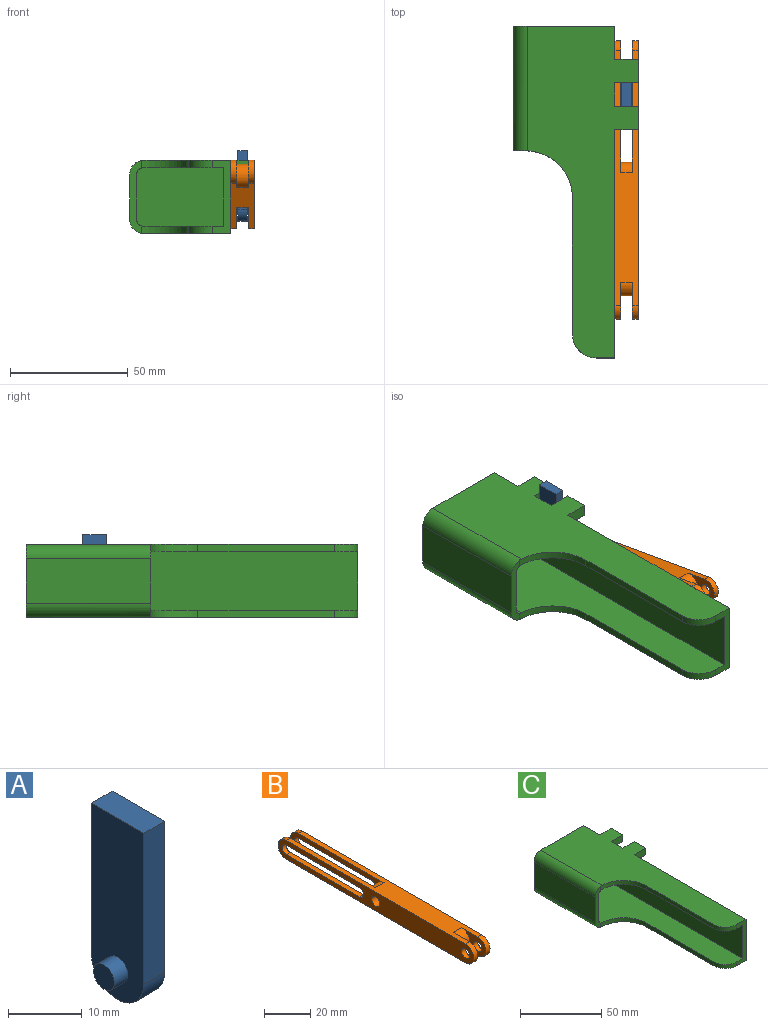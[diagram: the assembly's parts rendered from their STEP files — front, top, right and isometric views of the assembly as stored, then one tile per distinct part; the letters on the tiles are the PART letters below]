
ASSEMBLY  parts=3 mates=3
PART A: 10 faces, bbox 9.2x10x30 mm
  f0: plane 25x4mm, normal (0,1,0), area 100mm2, adj f1,f3,f4,f9
  f1: plane 30x10mm, normal (-1,0,0), area 276.7mm2, adj f0,f2,f4,f7,f9
  f2: plane 25x4mm, normal (0,-1,0), area 100mm2, adj f1,f3,f4,f9
  f3: plane 30x10mm, normal (1,0,0), area 276.7mm2, adj f0,f2,f4,f6,f9
  f4: plane 10x4mm, normal (0,0,1), area 40mm2, adj f0,f1,f2,f3
  f5: plane 4x4mm, normal (1,0,0), area 12.6mm2, adj f6
  f6: cylinder r=2mm len=4mm, axis (-1,0,0), area 32.7mm2, adj f3,f5
  f7: cylinder r=2mm len=4mm, axis (-1,0,0), area 32.7mm2, adj f1,f8
  f8: plane 4x4mm, normal (-1,0,0), area 12.6mm2, adj f7
  f9: cylinder r=5mm len=10mm, axis (-1,0,0), area 62.8mm2, adj f0,f1,f2,f3
PART B: 25 faces, bbox 10x120x10 mm
  f0: plane 110x10mm, normal (0,0,1), area 787.5mm2, adj f1,f2,f9,f15,f16,f17,f18,f19
  f1: cylinder r=5mm len=10mm, axis (-1,0,0), area 39.3mm2, adj f0,f3,f16,f20
  f2: cylinder r=5mm len=10mm, axis (-1,0,0), area 39.3mm2, adj f0,f3,f17,f21
  f3: plane 110x10mm, normal (0,0,-1), area 787.5mm2, adj f1,f2,f9,f15,f16,f17,f18,f19
  f4: cylinder r=2.5mm len=5mm, axis (-1,0,0), area 19.6mm2, adj f5,f7,f16,f18
  f5: plane 45x2.5mm, normal (0,0,-1), area 112.5mm2, adj f4,f6,f16,f18
  f6: cylinder r=2.5mm len=5mm, axis (-1,0,0), area 19.6mm2, adj f5,f7,f16,f18
  f7: plane 45x2.5mm, normal (0,0,1), area 112.5mm2, adj f4,f6,f16,f18
  f8: cylinder r=2.5mm len=5mm, axis (-1,0,0), area 39.3mm2, adj f16,f20
  f9: cylinder r=5mm len=10mm, axis (-1,0,0), area 39.3mm2, adj f0,f3,f16,f18
  f10: cylinder r=2.5mm len=5mm, axis (-1,0,0), area 19.6mm2, adj f11,f13,f17,f19
  f11: plane 45x2.5mm, normal (0,0,-1), area 112.5mm2, adj f10,f12,f17,f19
  f12: cylinder r=2.5mm len=5mm, axis (-1,0,0), area 19.6mm2, adj f11,f13,f17,f19
  f13: plane 45x2.5mm, normal (0,0,1), area 112.5mm2, adj f10,f12,f17,f19
  f14: cylinder r=2.5mm len=5mm, axis (-1,0,0), area 39.3mm2, adj f17,f21
  f15: cylinder r=5mm len=10mm, axis (-1,0,0), area 39.3mm2, adj f0,f3,f17,f19
  f16: plane 120x10mm, normal (1,0,0), area 894.6mm2, adj f0,f1,f3,f4,f5,f6,f7,f8
  f17: plane 120x10mm, normal (-1,0,0), area 894.6mm2, adj f0,f2,f3,f10,f11,f12,f13,f14
  f18: plane 57.5x10mm, normal (-1,0,0), area 280.4mm2, adj f0,f3,f4,f5,f6,f7,f9,f24
  f19: plane 57.5x10mm, normal (1,0,0), area 280.4mm2, adj f0,f3,f10,f11,f12,f13,f15,f24
  f20: plane 15x10mm, normal (-1,0,0), area 80.4mm2, adj f0,f1,f3,f8,f23
  f21: plane 15x10mm, normal (1,0,0), area 80.4mm2, adj f0,f2,f3,f14,f23
  f22: cylinder r=2.5mm len=10mm, axis (1,0,0), area 157.1mm2, adj f16,f17
  f23: cylinder r=5mm len=10mm, axis (-1,0,0), area 78.5mm2, adj f0,f3,f20,f21
  f24: cylinder r=5mm len=10mm, axis (1,0,0), area 78.5mm2, adj f0,f3,f18,f19
PART C: 32 faces, bbox 53x141x31 mm
  f0: plane 141x31mm, normal (1,0,0), area 4258.4mm2, adj f1,f2,f4,f5,f22,f24,f25,f26
  f1: plane 31x8mm, normal (0,-1,0), area 123mm2, adj f0,f4,f5,f10,f11,f12,f20,f21
  f2: plane 43x31mm, normal (0,1,0), area 1317.5mm2, adj f0,f3,f4,f5,f6,f7
  f3: plane 53x19mm, normal (-1,0,0), area 1007mm2, adj f2,f6,f7,f19
  f4: plane 141x47mm, normal (0,0,1), area 3809.4mm2, adj f0,f1,f2,f7,f16,f18,f20,f24
  f5: plane 141x37mm, normal (0,0,-1), area 3609.4mm2, adj f0,f1,f2,f6,f15,f17,f21
  f6: cylinder r=6mm len=53.03mm, axis (0,-1,0), area 499.5mm2, adj f2,f3,f5,f17,f19
  f7: cylinder r=6mm len=53.03mm, axis (0,1,0), area 499.5mm2, adj f2,f3,f4,f18,f19
  f8: plane 37x25mm, normal (0,-1,0), area 921.1mm2, adj f9,f10,f11,f12,f13,f14
  f9: plane 50x19mm, normal (1,0,0), area 950mm2, adj f8,f13,f14,f19
  f10: plane 138x25mm, normal (-1,0,0), area 3450mm2, adj f1,f8,f11,f12
  f11: plane 138x34mm, normal (0,0,-1), area 3084.4mm2, adj f1,f8,f10,f14,f16,f18,f20
  f12: plane 138x34mm, normal (0,0,1), area 3084.4mm2, adj f1,f8,f10,f13,f15,f17,f21
  f13: cylinder r=3mm len=50.03mm, axis (0,-1,0), area 235.6mm2, adj f8,f9,f12,f17,f19
  f14: cylinder r=3mm len=50.03mm, axis (0,1,0), area 235.6mm2, adj f8,f9,f11,f18,f19
  f15: plane 58x3mm, normal (-1,0,0), area 174mm2, adj f5,f12,f17,f21
  f16: plane 58x3mm, normal (-1,0,0), area 174mm2, adj f4,f11,f18,f20
  f17: cylinder r=20mm len=20mm, axis (0,0,1), area 94.3mm2, adj f5,f6,f12,f13,f15,f19
  f18: cylinder r=20mm len=20mm, axis (0,0,1), area 94.3mm2, adj f4,f7,f11,f14,f16,f19
  f19: plane 30.83x5mm, normal (0,-1,0), area 93.4mm2, adj f3,f6,f7,f9,f13,f14,f17,f18
  f20: cylinder r=10mm len=10mm, axis (0,0,1), area 47.1mm2, adj f1,f4,f11,f16
  f21: cylinder r=10mm len=10mm, axis (0,0,1), area 47.1mm2, adj f1,f5,f12,f15
  f22: cylinder r=2mm len=10mm, axis (-1,0,0), area 125.7mm2, adj f0,f23
  f23: plane 4x4mm, normal (1,0,0), area 12.6mm2, adj f22
  f24: plane 10x5mm, normal (0,-1,0), area 50mm2, adj f0,f4,f25,f27
  f25: plane 10x10mm, normal (0,0,-1), area 100mm2, adj f0,f24,f26,f27
  f26: plane 10x5mm, normal (0,1,0), area 50mm2, adj f0,f4,f25,f27
  f27: plane 10x5mm, normal (1,0,0), area 50mm2, adj f4,f24,f25,f26
  f28: plane 10x5mm, normal (0,-1,0), area 50mm2, adj f0,f4,f29,f31
  f29: plane 10x10mm, normal (0,0,-1), area 100mm2, adj f0,f28,f30,f31
  f30: plane 10x5mm, normal (0,1,0), area 50mm2, adj f0,f4,f29,f31
  f31: plane 10x5mm, normal (1,0,0), area 50mm2, adj f4,f28,f29,f30
PLACE A t=(50.51,121.21,5.23)mm
PLACE B rot(axis=(-1,0,0),10deg) t=(0,126.85,-38.38)mm
PLACE C t=(-107.6,141,0)mm
MATE pin_slot A.f6 <-> B.f6  axis (1,0,0) through (9.6,111.89,10.23)mm
MATE slider C.f4 <-> A.f4  axis (0,0,1) through (5,106.89,31)mm
MATE revolute B.f22 <-> C.f22  axis (1,0,0) through (10,75.63,16.62)mm
